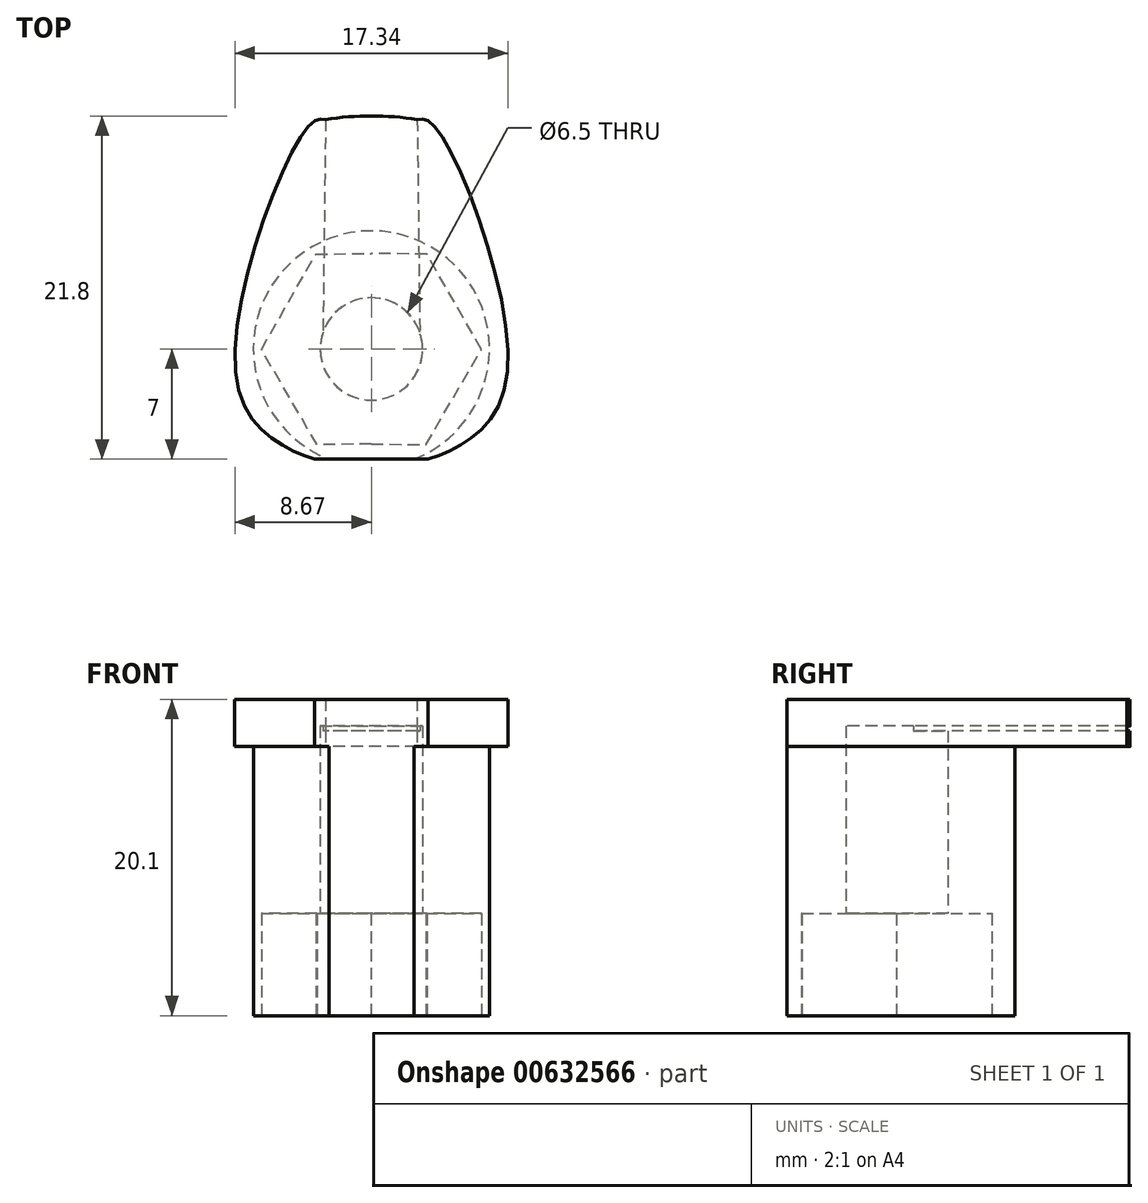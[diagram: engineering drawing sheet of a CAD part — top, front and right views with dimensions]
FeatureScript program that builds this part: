
annotation { "Feature Type Name" : "Feature", "Feature Type Description" : "" }
export const myFeature = defineFeature(function(context is Context, id is Id, definition is map)
    precondition{}
    {
        {
            var Q0;
            Q0=qCreatedBy(makeId("Top.planeOp"),FACE);
            var sketch = newSketch(context, id + "F0", { "sketchPlane" : qUnion([Q0])});
            skCircle(sketch, "E0.cCircle", {"center": v(0, 0) * mm, "radius": 6.05 * mm, "construction": true});
            skLineSegment(sketch, "E0.0", {"start": v(3.46, 6.07) * mm, "end": v(6.99, 0.04) * mm});
            skLineSegment(sketch, "E0.1", {"start": v(6.99, 0.04) * mm, "end": v(3.53, -6.03) * mm});
            skLineSegment(sketch, "E0.2", {"start": v(3.53, -6.03) * mm, "end": v(-3.46, -6.07) * mm});
            skLineSegment(sketch, "E0.3", {"start": v(-3.46, -6.07) * mm, "end": v(-6.99, -0.04) * mm});
            skLineSegment(sketch, "E0.4", {"start": v(-6.99, -0.04) * mm, "end": v(-3.53, 6.03) * mm});
            skLineSegment(sketch, "E0.5", {"start": v(-3.53, 6.03) * mm, "end": v(3.46, 6.07) * mm});
            skPoint(sketch, "E0.0.midPoint", {"position": v(5.22, 3.05) * mm});
            skCircle(sketch, "E1", {"center": v(0, 0) * mm, "radius": 7.5 * mm});
            skSolve(sketch);
        }
        {
            var Q0;
            Q0=makeQuery(id+"F0.imprint","IMPRINT",FACE,{"disambiguationData":[TD([[makeQuery(id+"F0.imprint","IMPRINT",EDGE,{"derivedFrom":sQuery(id+"F0.wireOp",EDGE,"E0.0")}),1.0]])]});
            extrude(context, id + "F1", {"entities" : qUnion([Q0]), "depth" : 6.5 * mm, "offsetDistance" : 25 * mm});
        }
        {
            var Q0;
            Q0=makeQuery(id+"F1.opExtrude","CAP_FACE",FACE,{"disambiguationData":[OSD([sQuery(id+"F0.wireOp",EDGE,"E0.0"),sQuery(id+"F0.wireOp",EDGE,"E0.1"),sQuery(id+"F0.wireOp",EDGE,"E0.2"),sQuery(id+"F0.wireOp",EDGE,"E0.3"),sQuery(id+"F0.wireOp",EDGE,"E0.4"),sQuery(id+"F0.wireOp",EDGE,"E0.5"),sQuery(id+"F0.wireOp",EDGE,"E1")])],"isStart":false});
            cPlane(context, id + "F2", {"entities" : qUnion([Q0]), "cplaneType" : CPlaneType.OFFSET, "offset" : 0 * mm, "width" : 150 * mm, "height" : 150 * mm});
        }
        {
            var Q0;
            Q0=qCreatedBy(id+"F2.planeOp",FACE);
            var sketch = newSketch(context, id + "F3", { "sketchPlane" : qUnion([Q0])});
            skCircle(sketch, "E2", {"center": v(0, 0) * mm, "radius": 7.5 * mm});
            skCircle(sketch, "E3", {"center": v(0, 0) * mm, "radius": 3.25 * mm});
            skSolve(sketch);
        }
        {
            var Q0;
            Q0=makeQuery(id+"F3.imprint","IMPRINT",FACE,{"disambiguationData":[TD([[makeQuery(id+"F3.imprint","IMPRINT",EDGE,{"derivedFrom":sQuery(id+"F3.wireOp",EDGE,"E2")}),1.0]])]});
            extrude(context, id + "F4", {"entities" : qUnion([Q0]), "operationType" : NewBodyOperationType.ADD, "depth" : 10.6 * mm, "offsetDistance" : 25 * mm});
        }
        {
            var Q0;
            Q0=makeQuery(id+"F4.opExtrude","CAP_FACE",FACE,{"disambiguationData":[OSD([sQuery(id+"F3.wireOp",EDGE,"E2"),sQuery(id+"F3.wireOp",EDGE,"E3")])],"isStart":false});
            cPlane(context, id + "F5", {"entities" : qUnion([Q0]), "cplaneType" : CPlaneType.OFFSET, "offset" : 0 * mm, "width" : 150 * mm, "height" : 150 * mm});
        }
        {
            var Q0;
            Q0=qCreatedBy(id+"F5.planeOp",FACE);
            var sketch = newSketch(context, id + "F6", { "sketchPlane" : qUnion([Q0])});
            skLineSegment(sketch, "E4", {"start": v(0, 0) * mm, "end": v(-7.5, 0) * mm, "construction": true});
            skLineSegment(sketch, "E5", {"start": v(0, 0) * mm, "end": v(3.25, 0) * mm, "construction": true});
            skLineSegment(sketch, "E6", {"start": v(0, 0) * mm, "end": v(0, -7.5) * mm, "construction": true});
            skCircle(sketch, "E7", {"center": v(0, 0) * mm, "radius": 3.25 * mm});
            skPoint(sketch, "E8.endSnap0", {"position": v(2.91, 4.94) * mm});
            skLineSegment(sketch, "E9", {"start": v(0, -7.5) * mm, "end": v(1.7, -7.5) * mm});
            skFitSpline(sketch, "E10", {"points": [v(1.7, -7.5) * mm, v(5.19, -6.37) * mm, v(8.65, -1.31) * mm, v(3.96, 14.2) * mm, v(2.91, 14.58) * mm], "startDerivative": vector(16.92, 3.95) * mm, "endDerivative": vector(-8.28, -1.01) * mm});
            skFitSpline(sketch, "E11.MirrorCS", {"points": [v(-1.7, -7.5) * mm, v(-5.19, -6.37) * mm, v(-8.65, -1.31) * mm, v(-3.96, 14.2) * mm, v(-2.91, 14.58) * mm], "startDerivative": vector(-16.92, 3.95) * mm, "endDerivative": vector(8.28, -1.01) * mm});
            skLineSegment(sketch, "E12.MirrorCS", {"start": v(0, -7.5) * mm, "end": v(-1.7, -7.5) * mm});
            skArc(sketch, "E13", {"start": v(2.91, 14.58) * mm, "mid": v(0, 14.8) * mm, "end": v(-2.91, 14.58) * mm});
            skLineSegment(sketch, "E14", {"start": v(2.91, 14.58) * mm, "end": v(3.08, 1.05) * mm});
            skLineSegment(sketch, "E15.MirrorCS", {"start": v(-2.91, 14.58) * mm, "end": v(-3.08, 1.05) * mm});
            skPoint(sketch, "E16", {"position": v(3, 7.38) * mm});
            skSolve(sketch);
        }
        {
            var Q0;
            Q0=makeQuery(id+"F0.imprint","IMPRINT",FACE,{"disambiguationData":[TD([[makeQuery(id+"F0.imprint","IMPRINT",EDGE,{"derivedFrom":sQuery(id+"F0.wireOp",EDGE,"E0.0")}),1.0]])]});
            cPlane(context, id + "F7", {"entities" : qUnion([Q0]), "cplaneType" : CPlaneType.OFFSET, "offset" : 0 * mm, "width" : 150 * mm, "height" : 150 * mm});
        }
        {
            var Q0;
            Q0=qCreatedBy(id+"F7.planeOp",FACE);
            var sketch = newSketch(context, id + "F8", { "sketchPlane" : qUnion([Q0])});
            skLineSegment(sketch, "E17", {"start": v(0, 0) * mm, "end": v(0, -7) * mm, "construction": true});
            skLineSegment(sketch, "E18", {"start": v(0, -7) * mm, "end": v(5.15, -7) * mm});
            skLineSegment(sketch, "E19", {"start": v(5.15, -7) * mm, "end": v(5.15, -7.55) * mm});
            skLineSegment(sketch, "E20", {"start": v(5.15, -7.55) * mm, "end": v(-6.58, -7.55) * mm});
            skLineSegment(sketch, "E21", {"start": v(-6.58, -7.55) * mm, "end": v(-6.58, -7) * mm});
            skLineSegment(sketch, "E22", {"start": v(-6.58, -7) * mm, "end": v(0, -7) * mm});
            skSolve(sketch);
        }
        {
            var Q0;
            Q0=qCreatedBy(makeId("Top.planeOp"),FACE);
            var sketch = newSketch(context, id + "F9", { "sketchPlane" : qUnion([Q0])});
            skLineSegment(sketch, "E23.bottom", {"start": v(0, -8.32) * mm, "end": v(19.03, -8.32) * mm});
            skLineSegment(sketch, "E23.top", {"start": v(0, 21.36) * mm, "end": v(19.03, 21.36) * mm});
            skLineSegment(sketch, "E23.left", {"start": v(0, -8.32) * mm, "end": v(0, 21.36) * mm});
            skLineSegment(sketch, "E23.right", {"start": v(19.03, -8.32) * mm, "end": v(19.03, 21.36) * mm});
            skSolve(sketch);
        }
        {
            var Q0;
            Q0=makeQuery(id+"F9.imprint","IMPRINT",FACE,{"disambiguationData":[TD([[makeQuery(id+"F9.imprint","IMPRINT",EDGE,{"derivedFrom":sQuery(id+"F9.wireOp",EDGE,"E23.bottom")}),1.0]])]});
            extrude(context, id + "F10", {"entities" : qUnion([Q0]), "operationType" : NewBodyOperationType.REMOVE, "depth" : 25 * mm, "offsetDistance" : 25 * mm});
        }
        {
            var Q0;
            Q0 = qSketchRegion(id + "F6", true);
            var Q1;
            {var subQ0=sQuery(id+"F6.wireOp",EDGE,"E7");var subQ1=makeQuery(id+"F6.imprint","INTERSECT",VERTEX,{"derivedFrom":[subQ0,sQuery(id+"F6.wireOp",EDGE,"E14")]});Q1=makeQuery(id+"F6.imprint","IMPRINT",FACE,{"disambiguationData":[TD([[makeQuery(id+"F6.imprint","IMPRINT",EDGE,{"disambiguationData":[TD([[subQ1,-1.0]])],"derivedFrom":subQ0}),1.0]])]});}
            extrude(context, id + "F11", {"entities" : qUnion([Q0, Q1]), "operationType" : NewBodyOperationType.ADD, "depth" : 3 * mm, "offsetDistance" : 25 * mm});
        }
        {
            var Q0;
            Q0=makeQuery(id+"F6.imprint","IMPRINT",FACE,{"disambiguationData":[TD([[makeQuery(id+"F6.imprint","IMPRINT",EDGE,{"derivedFrom":sQuery(id+"F6.wireOp",EDGE,"E13")}),1.0]])]});
            var Q1;
            {var subQ0=sQuery(id+"F6.wireOp",EDGE,"E7");var subQ1=makeQuery(id+"F6.imprint","INTERSECT",VERTEX,{"derivedFrom":[subQ0,sQuery(id+"F6.wireOp",EDGE,"E14")]});Q1=makeQuery(id+"F6.imprint","IMPRINT",FACE,{"disambiguationData":[TD([[makeQuery(id+"F6.imprint","IMPRINT",EDGE,{"disambiguationData":[TD([[subQ1,-1.0]])],"derivedFrom":subQ0}),1.0]])]});}
            extrude(context, id + "F12", {"entities" : qUnion([Q0, Q1]), "operationType" : NewBodyOperationType.REMOVE, "depth" : 1.3 * mm, "offsetDistance" : 25 * mm});
        }
        {
            var Q0;
            Q0=makeQuery(id+"F6.imprint","IMPRINT",FACE,{"disambiguationData":[TD([[makeQuery(id+"F6.imprint","IMPRINT",EDGE,{"derivedFrom":sQuery(id+"F6.wireOp",EDGE,"E13")}),1.0]])]});
            extrude(context, id + "F13", {"entities" : qUnion([Q0]), "operationType" : NewBodyOperationType.ADD, "depth" : 1 * mm, "offsetDistance" : 25 * mm});
        }
        {
            var Q0;
            Q0=makeQuery(id+"F1.opExtrude","SWEPT_BODY",BODY,{"disambiguationData":[OSD([sQuery(id+"F0.wireOp",EDGE,"E0.0"),sQuery(id+"F0.wireOp",EDGE,"E0.1"),sQuery(id+"F0.wireOp",EDGE,"E0.2"),sQuery(id+"F0.wireOp",EDGE,"E0.3"),sQuery(id+"F0.wireOp",EDGE,"E0.4"),sQuery(id+"F0.wireOp",EDGE,"E0.5"),sQuery(id+"F0.wireOp",EDGE,"E1")])]});
            var Q1;
            {var subQ3=sQuery(id+"F0.wireOp",EDGE,"E0.5");Q1=makeQuery(id+"F10.boolean.opBoolean","COPY",FACE,{"disambiguationData":[TD([makeQuery(id+"F1.opExtrude","SWEPT_FACE",FACE,{"disambiguationData":[OSD([subQ3])]})])],"derivedFrom":makeQuery(id+"F10.opExtrude","SWEPT_FACE",FACE,{"disambiguationData":[OSD([sQuery(id+"F9.wireOp",EDGE,"E23.left")])]})});}
            mirror(context, id + "F14", {"operationType" : NewBodyOperationType.ADD, "entities" : qUnion([Q0]), "mirrorPlane" : qUnion([Q1])});
        }
        {
            var Q0;
            Q0 = qSketchRegion(id + "F8", true);
            extrude(context, id + "F15", {"entities" : qUnion([Q0]), "operationType" : NewBodyOperationType.REMOVE, "depth" : 25 * mm, "offsetDistance" : 25 * mm});
        }
    });
